# Revit family: Sink-Vessel-Lavatory-KOHLER-K-14223T_1
name_source: partatom
category: Plumbing Fixtures
revit_build: Autodesk Revit 2017 (Build: 20160225_1515(x64)
units: mm (PartAtom-declared; Revit-internal decimal feet)

## family parameters
Cut with Voids When Loaded = No
Host = Face
OmniClass Number = 23.31.13.00
OmniClass Title = Sinks
Part Type = Normal
Room Calculation Point = No
Round Connector Dimension = Use Diameter
Shared = No

## types (3) — shared parameters
ADA Compliant = Yes
Assembly Code = D2010400
CW Connection = No
Cold Water Inlet = Cold Water Inlet
Date Modified = 05/26/2020
Default Elevation = 34"
Description = Vessels Lavatory
Drain Included = No
HW Connection = No
Height = 6 3/8"
Hot Water Inlet = Hot Water Inlet
Length = 16 1/4"
Manufacturer = KOHLER Co.
MasterFormat 1995 = 15410
MasterFormat 2004 = 22.41.16
Material = Vitreous China
Product Documentation Link = http://files.kohler.com.cn
Product Page URL = http://www.kohler.com.cn
URL = http://www.kohler.com.cn
Vent Connection = No
Waste Connection = Yes
Waste Water Outlet = Waste Water Outlet
WaterSense Certified = No
Width = 16 1/4"

## per-type parameters (varying)
| type | Finish | Model | Type |
| G4, 0-White | Kohler-Vitreous_China-0-White | K-14223T-G4-0 | 1 |
| GB, 96-Biscuit | Kohler-Vitreous_China-96-Biscuit | K-14223T-GB-96 | 2 |
| SMC, 0-White | Kohler-Vitreous_China-0-White | K-14223T-SMC-0 | 3 |

## geometry (parser evidence)
native form markers: Sweep x6
no freeform markers — native parametric forms only
